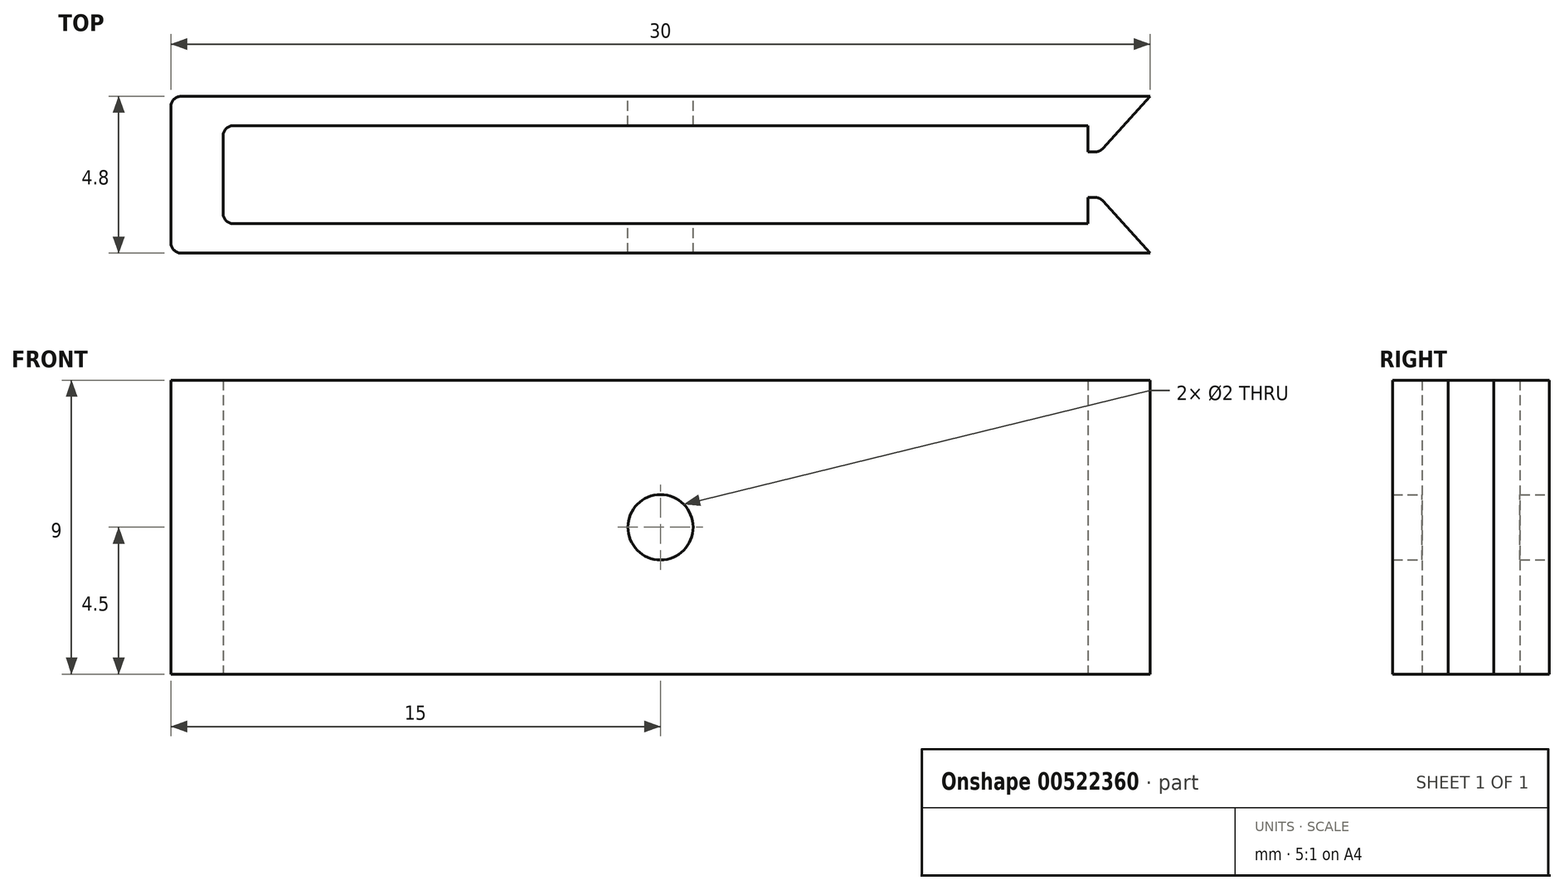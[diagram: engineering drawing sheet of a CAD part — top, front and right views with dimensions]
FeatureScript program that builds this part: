
annotation { "Feature Type Name" : "Feature", "Feature Type Description" : "" }
export const myFeature = defineFeature(function(context is Context, id is Id, definition is map)
    precondition{}
    {
        {
            var Q0;
            Q0=qCreatedBy(makeId("Top.planeOp"),FACE);
            var sketch = newSketch(context, id + "F0", { "sketchPlane" : qUnion([Q0])});
            skLineSegment(sketch, "E0.bottom", {"start": v(15, -2.4) * mm, "end": v(-14.69, -2.4) * mm});
            skLineSegment(sketch, "E0.top", {"start": v(15, 2.4) * mm, "end": v(-14.69, 2.4) * mm});
            skLineSegment(sketch, "E0.right", {"start": v(-15, -2.09) * mm, "end": v(-15, 2.09) * mm});
            skPoint(sketch, "E0.middle", {"position": v(0, 0) * mm});
            skLineSegment(sketch, "E1.bottom", {"start": v(13.1, 1.5) * mm, "end": v(-13.09, 1.5) * mm});
            skLineSegment(sketch, "E1.top", {"start": v(13.1, -1.5) * mm, "end": v(-13.09, -1.5) * mm});
            skLineSegment(sketch, "E1.right", {"start": v(-13.4, 1.19) * mm, "end": v(-13.4, -1.19) * mm});
            skLineSegment(sketch, "E2", {"start": v(15, 0) * mm, "end": v(-15, 0) * mm, "construction": true});
            skLineSegment(sketch, "E3.top", {"start": v(13.32, 0.7) * mm, "end": v(13.1, 0.7) * mm});
            skLineSegment(sketch, "E3.right", {"start": v(13.1, 1.5) * mm, "end": v(13.1, 0.7) * mm});
            skLineSegment(sketch, "E4", {"start": v(13.55, 0.8) * mm, "end": v(15, 2.4) * mm});
            skLineSegment(sketch, "E5", {"start": v(13.1, -1.5) * mm, "end": v(13.1, -0.7) * mm});
            skLineSegment(sketch, "E6", {"start": v(13.1, -0.7) * mm, "end": v(13.32, -0.7) * mm});
            skLineSegment(sketch, "E7", {"start": v(13.55, -0.8) * mm, "end": v(15, -2.4) * mm});
            skPoint(sketch, "E8.visualSharp", {"position": v(-15, 2.4) * mm});
            skArc(sketch, "E8.filletArc", {"start": v(-14.69, 2.4) * mm, "mid": v(-14.9, 2.3) * mm, "end": v(-15, 2.09) * mm});
            skPoint(sketch, "E9.visualSharp", {"position": v(-15, -2.4) * mm});
            skArc(sketch, "E9.filletArc", {"start": v(-15, -2.09) * mm, "mid": v(-14.9, -2.3) * mm, "end": v(-14.69, -2.4) * mm});
            skPoint(sketch, "E10.visualSharp", {"position": v(-13.4, 1.5) * mm});
            skArc(sketch, "E10.filletArc", {"start": v(-13.09, 1.5) * mm, "mid": v(-13.3, 1.4) * mm, "end": v(-13.4, 1.19) * mm});
            skPoint(sketch, "E11.visualSharp", {"position": v(-13.4, -1.5) * mm});
            skArc(sketch, "E11.filletArc", {"start": v(-13.4, -1.19) * mm, "mid": v(-13.3, -1.4) * mm, "end": v(-13.09, -1.5) * mm});
            skPoint(sketch, "E12.visualSharp", {"position": v(13.46, -0.7) * mm});
            skArc(sketch, "E12.filletArc", {"start": v(13.55, -0.8) * mm, "mid": v(13.45, -0.73) * mm, "end": v(13.32, -0.7) * mm});
            skPoint(sketch, "E13.visualSharp", {"position": v(13.46, 0.7) * mm});
            skArc(sketch, "E13.filletArc", {"start": v(13.32, 0.7) * mm, "mid": v(13.45, 0.73) * mm, "end": v(13.55, 0.8) * mm});
            skSolve(sketch);
        }
        {
            var Q0;
            Q0=makeQuery(id+"F0.imprint","IMPRINT",FACE,{"disambiguationData":[TD([[makeQuery(id+"F0.imprint","IMPRINT",EDGE,{"derivedFrom":sQuery(id+"F0.wireOp",EDGE,"E0.bottom")}),-1.0]])]});
            extrude(context, id + "F1", {"entities" : qUnion([Q0]), "depth" : 9 * mm, "offsetDistance" : 25 * mm});
        }
        {
            var Q0;
            Q0=makeQuery(id+"F1.opExtrude","SWEPT_FACE",FACE,{"disambiguationData":[OSD([sQuery(id+"F0.wireOp",EDGE,"E0.top")])]});
            var sketch = newSketch(context, id + "F2", { "sketchPlane" : qUnion([Q0])});
            skLineSegment(sketch, "E14", {"start": v(14.69, 4.5) * mm, "end": v(-15, 4.5) * mm, "construction": true});
            skLineSegment(sketch, "E15", {"start": v(0, 9) * mm, "end": v(0, 0) * mm, "construction": true});
            skCircle(sketch, "E16", {"center": v(0, 4.5) * mm, "radius": 1 * mm});
            skSolve(sketch);
        }
        {
            var Q0;
            Q0=makeQuery(id+"F2.imprint","IMPRINT",FACE,{"disambiguationData":[TD([[makeQuery(id+"F2.imprint","IMPRINT",EDGE,{"derivedFrom":sQuery(id+"F2.wireOp",EDGE,"E16")}),1.0]])]});
            extrude(context, id + "F3", {"entities" : qUnion([Q0]), "operationType" : NewBodyOperationType.REMOVE, "endBound" : BoundingType.THROUGH_ALL, "oppositeDirection" : true, "depth" : 3 * mm, "offsetDistance" : 25 * mm});
        }
    });
